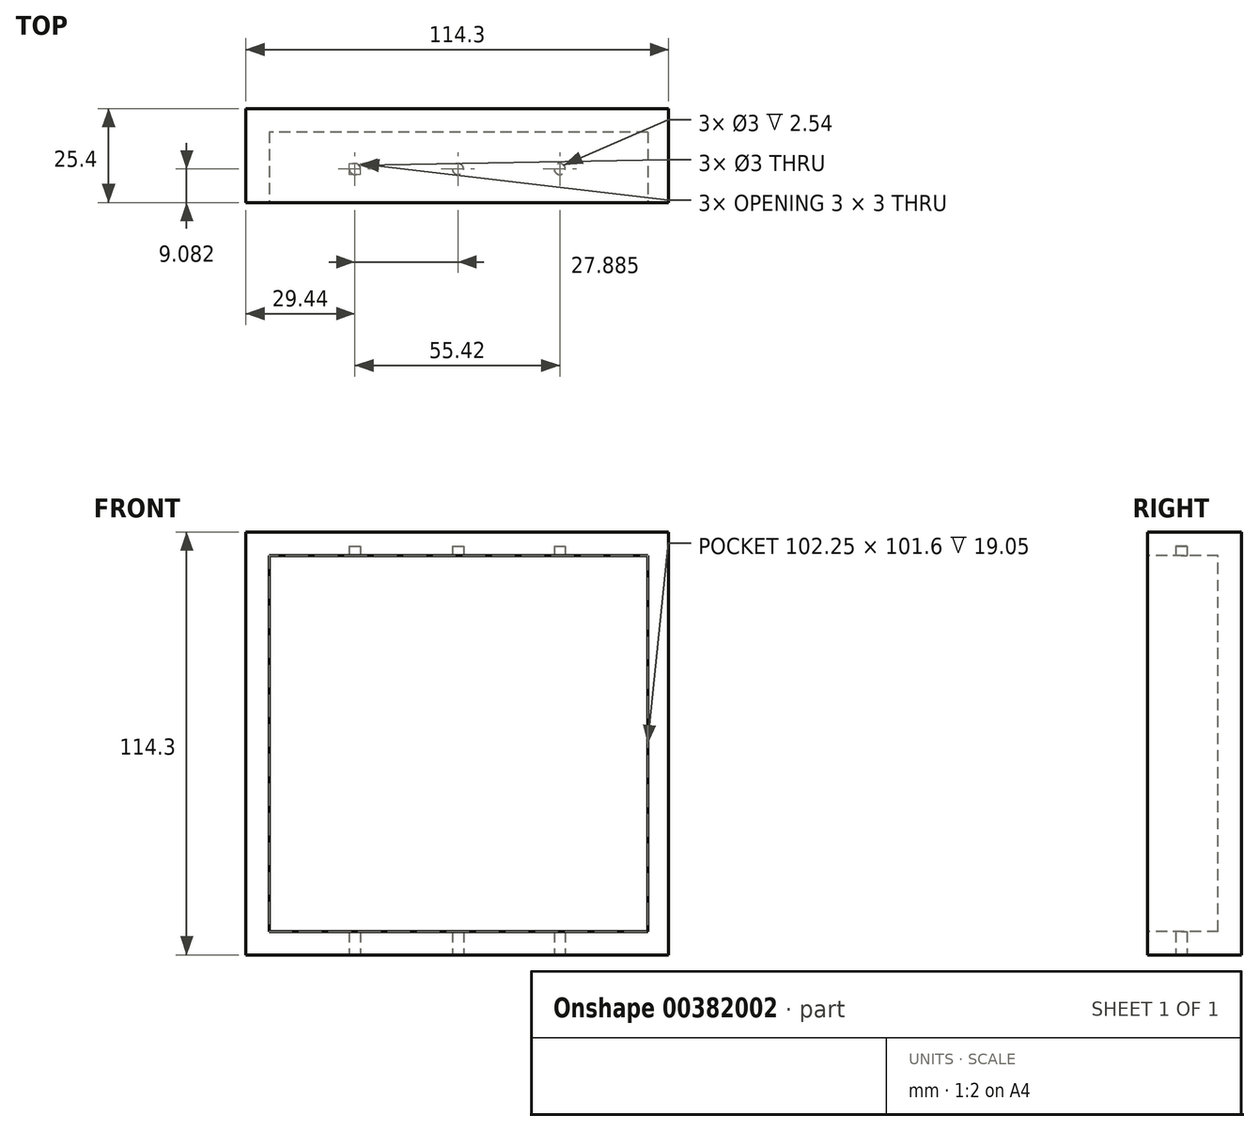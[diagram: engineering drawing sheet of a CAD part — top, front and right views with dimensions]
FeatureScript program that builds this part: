
annotation { "Feature Type Name" : "Feature", "Feature Type Description" : "" }
export const myFeature = defineFeature(function(context is Context, id is Id, definition is map)
    precondition{}
    {
        {
            var Q0;
            Q0=qCreatedBy(makeId("Front.planeOp"),FACE);
            var sketch = newSketch(context, id + "F0", { "sketchPlane" : qUnion([Q0])});
            skLineSegment(sketch, "E0.bottom", {"start": v(57.15, -57.15) * mm, "end": v(-57.15, -57.15) * mm});
            skLineSegment(sketch, "E0.top", {"start": v(57.15, 57.15) * mm, "end": v(-57.15, 57.15) * mm});
            skLineSegment(sketch, "E0.left", {"start": v(57.15, -57.15) * mm, "end": v(57.15, 57.15) * mm});
            skLineSegment(sketch, "E0.right", {"start": v(-57.15, -57.15) * mm, "end": v(-57.15, 57.15) * mm});
            skPoint(sketch, "E0.middle", {"position": v(0, 0) * mm});
            skSolve(sketch);
        }
        {
            var Q0;
            Q0=makeQuery(id+"F0.imprint","IMPRINT",FACE,{"disambiguationData":[TD([[makeQuery(id+"F0.imprint","IMPRINT",EDGE,{"derivedFrom":sQuery(id+"F0.wireOp",EDGE,"E0.bottom")}),-1.0]])]});
            var sketch = newSketch(context, id + "F1", { "sketchPlane" : qUnion([Q0])});
            skSolve(sketch);
        }
        {
            var Q0;
            Q0 = qSketchRegion(id + "F1", true);
            var Q1;
            Q1=makeQuery(id+"F0.imprint","IMPRINT",FACE,{"disambiguationData":[TD([[makeQuery(id+"F0.imprint","IMPRINT",EDGE,{"derivedFrom":sQuery(id+"F0.wireOp",EDGE,"E0.bottom")}),-1.0]])]});
            extrude(context, id + "F2", {"entities" : qUnion([Q0, Q1]), "depth" : 25.4 * mm});
        }
        {
            var Q0;
            Q0=makeQuery(id+"F2.opExtrude","CAP_FACE",FACE,{"disambiguationData":[OSD([sQuery(id+"F0.wireOp",EDGE,"E0.bottom"),sQuery(id+"F0.wireOp",EDGE,"E0.top"),sQuery(id+"F0.wireOp",EDGE,"E0.left"),sQuery(id+"F0.wireOp",EDGE,"E0.right")])],"isStart":false});
            var sketch = newSketch(context, id + "F3", { "sketchPlane" : qUnion([Q0])});
            skLineSegment(sketch, "E1.bottom", {"start": v(51.45, -50.8) * mm, "end": v(-50.8, -50.8) * mm});
            skLineSegment(sketch, "E1.top", {"start": v(51.45, 50.8) * mm, "end": v(-50.8, 50.8) * mm});
            skLineSegment(sketch, "E1.left", {"start": v(51.45, -50.8) * mm, "end": v(51.45, 50.8) * mm});
            skLineSegment(sketch, "E1.right", {"start": v(-50.8, -50.8) * mm, "end": v(-50.8, 50.8) * mm});
            skPoint(sketch, "E1.middle", {"position": v(0.33, 0) * mm});
            skSolve(sketch);
        }
        {
            var Q0;
            Q0=makeQuery(id+"F3.imprint","IMPRINT",FACE,{"disambiguationData":[TD([[makeQuery(id+"F3.imprint","IMPRINT",EDGE,{"derivedFrom":sQuery(id+"F3.wireOp",EDGE,"E1.bottom")}),-1.0]])]});
            extrude(context, id + "F4", {"entities" : qUnion([Q0]), "operationType" : NewBodyOperationType.REMOVE, "oppositeDirection" : true, "depth" : 19.05 * mm});
        }
        {
            var Q0;
            Q0=makeQuery(id+"F2.opExtrude","SWEPT_FACE",FACE,{"disambiguationData":[OSD([sQuery(id+"F0.wireOp",EDGE,"E0.bottom")])]});
            var sketch = newSketch(context, id + "F5", { "sketchPlane" : qUnion([Q0])});
            skCircle(sketch, "E2", {"center": v(-27.71, 16.32) * mm, "radius": 1.5 * mm});
            skCircle(sketch, "E3", {"center": v(0.17, 16.32) * mm, "radius": 1.5 * mm});
            skCircle(sketch, "E4", {"center": v(27.7, 16.32) * mm, "radius": 1.5 * mm});
            skSolve(sketch);
        }
        {
            var Q0;
            Q0=makeQuery(id+"F5.imprint","IMPRINT",FACE,{"disambiguationData":[TD([[makeQuery(id+"F5.imprint","IMPRINT",EDGE,{"derivedFrom":sQuery(id+"F5.wireOp",EDGE,"E3")}),1.0]])]});
            var Q1;
            Q1=makeQuery(id+"F5.imprint","IMPRINT",FACE,{"disambiguationData":[TD([[makeQuery(id+"F5.imprint","IMPRINT",EDGE,{"derivedFrom":sQuery(id+"F5.wireOp",EDGE,"E4")}),1.0]])]});
            var Q2;
            Q2=makeQuery(id+"F5.imprint","IMPRINT",FACE,{"disambiguationData":[TD([[makeQuery(id+"F5.imprint","IMPRINT",EDGE,{"derivedFrom":sQuery(id+"F5.wireOp",EDGE,"E2")}),1.0]])]});
            var Q3;
            Q3=sQuery(id+"F5.wireOp",EDGE,"E2");
            var Q4;
            Q4=sQuery(id+"F5.wireOp",EDGE,"E3");
            var Q5;
            Q5=sQuery(id+"F5.wireOp",EDGE,"E4");
            extrude(context, id + "F6", {"entities" : qUnion([Q0, Q1, Q2]), "operationType" : NewBodyOperationType.REMOVE, "surfaceEntities" : qUnion([Q3, Q4, Q5]), "oppositeDirection" : true, "depth" : 110.49 * mm});
        }
    });
